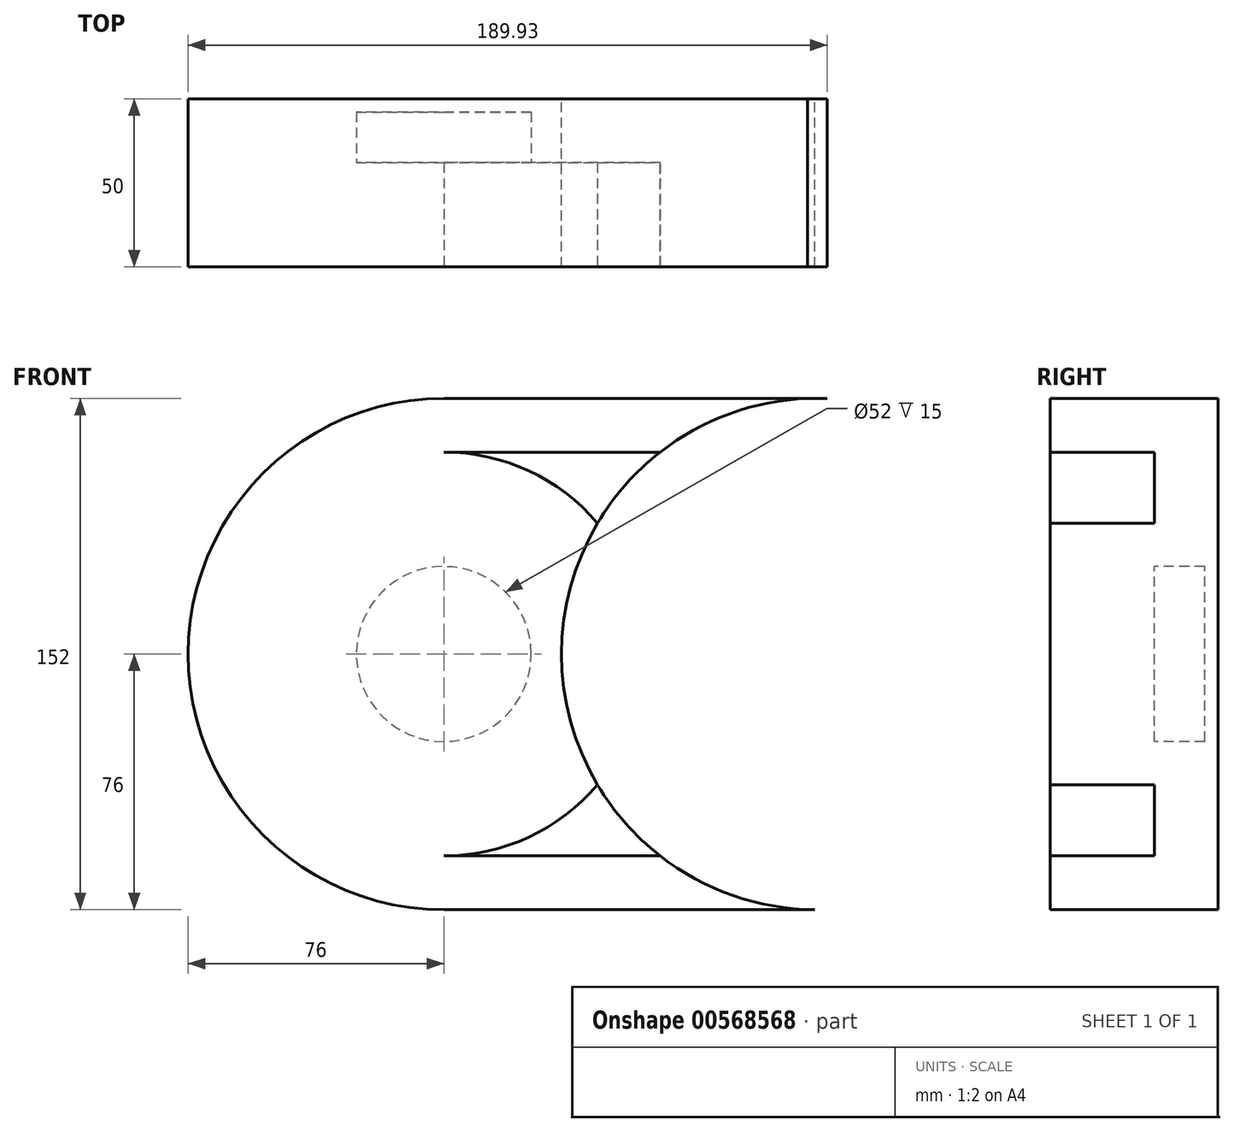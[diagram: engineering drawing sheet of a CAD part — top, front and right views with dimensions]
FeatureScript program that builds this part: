
annotation { "Feature Type Name" : "Feature", "Feature Type Description" : "" }
export const myFeature = defineFeature(function(context is Context, id is Id, definition is map)
    precondition{}
    {
        {
            var Q0;
            Q0=qCreatedBy(makeId("Front.planeOp"),FACE);
            var sketch = newSketch(context, id + "F0", { "sketchPlane" : qUnion([Q0])});
            skCircle(sketch, "E0", {"center": v(0, 0) * mm, "radius": 76 * mm});
            skCircle(sketch, "E1", {"center": v(111, 0) * mm, "radius": 76 * mm});
            skLineSegment(sketch, "E2", {"start": v(0, 76) * mm, "end": v(113.93, 75.94) * mm});
            skLineSegment(sketch, "E3", {"start": v(111.66, -76) * mm, "end": v(0, -76) * mm});
            skLineSegment(sketch, "E4", {"start": v(0, 0) * mm, "end": v(111, 0) * mm, "construction": true});
            skSolve(sketch);
        }
        {
            var Q0;
            {var subQ0=sQuery(id+"F0.wireOp",EDGE,"E3");var subQ1=sQuery(id+"F0.wireOp",EDGE,"E0");var subQ2=makeQuery(id+"F0.imprint","INTERSECT",VERTEX,{"derivedFrom":[subQ1,subQ0]});Q0=makeQuery(id+"F0.imprint","IMPRINT",FACE,{"disambiguationData":[TD([[makeQuery(id+"F0.imprint","IMPRINT",EDGE,{"disambiguationData":[TD([[subQ2,-1.0]])],"derivedFrom":subQ1}),-1.0]])]});}
            var Q1;
            {var subQ0=sQuery(id+"F0.wireOp",EDGE,"E0");var subQ1=makeQuery(id+"F0.imprint","INTERSECT",VERTEX,{"derivedFrom":[subQ0,sQuery(id+"F0.wireOp",EDGE,"E2")]});Q1=makeQuery(id+"F0.imprint","IMPRINT",FACE,{"disambiguationData":[TD([[makeQuery(id+"F0.imprint","IMPRINT",EDGE,{"disambiguationData":[TD([[subQ1,1.0]])],"derivedFrom":subQ0}),1.0]])]});}
            var Q2;
            {var subQ0=sQuery(id+"F0.wireOp",EDGE,"E1");var subQ2=sQuery(id+"F0.wireOp",EDGE,"E0");var subQ6=makeQuery(id+"F0.imprint","INTERSECT",VERTEX,{"disambiguationData":[OD(0.0)],"derivedFrom":[subQ2,subQ0]});Q2=makeQuery(id+"F0.imprint","IMPRINT",FACE,{"disambiguationData":[TD([[makeQuery(id+"F0.imprint","IMPRINT",EDGE,{"disambiguationData":[TD([[subQ6,1.0]])],"derivedFrom":subQ2}),-1.0]])]});}
            var Q3;
            {var subQ0=sQuery(id+"F0.wireOp",EDGE,"E2");var subQ1=sQuery(id+"F0.wireOp",EDGE,"E1");var subQ2=makeQuery(id+"F0.imprint","INTERSECT",VERTEX,{"disambiguationData":[OD(0.0)],"derivedFrom":[subQ1,subQ0]});Q3=makeQuery(id+"F0.imprint","IMPRINT",FACE,{"disambiguationData":[TD([[makeQuery(id+"F0.imprint","IMPRINT",EDGE,{"disambiguationData":[TD([[subQ2,-1.0]])],"derivedFrom":subQ1}),1.0]])]});}
            var Q4;
            {var subQ0=sQuery(id+"F0.wireOp",EDGE,"E2");var subQ1=sQuery(id+"F0.wireOp",EDGE,"E0");var subQ2=makeQuery(id+"F0.imprint","INTERSECT",VERTEX,{"derivedFrom":[subQ1,subQ0]});Q4=makeQuery(id+"F0.imprint","IMPRINT",FACE,{"disambiguationData":[TD([[makeQuery(id+"F0.imprint","IMPRINT",EDGE,{"disambiguationData":[TD([[subQ2,1.0]])],"derivedFrom":subQ1}),-1.0]])]});}
            var Q5;
            {var subQ0=sQuery(id+"F0.wireOp",EDGE,"E1");var subQ1=sQuery(id+"F0.wireOp",EDGE,"E0");var subQ2=makeQuery(id+"F0.imprint","INTERSECT",VERTEX,{"disambiguationData":[OD(0.0)],"derivedFrom":[subQ1,subQ0]});Q5=makeQuery(id+"F0.imprint","IMPRINT",FACE,{"disambiguationData":[TD([[makeQuery(id+"F0.imprint","IMPRINT",EDGE,{"disambiguationData":[TD([[subQ2,1.0]])],"derivedFrom":subQ1}),1.0]])]});}
            extrude(context, id + "F1", {"entities" : qUnion([Q0, Q1, Q2, Q3, Q4, Q5]), "depth" : 50 * mm, "offsetDistance" : 25 * mm});
        }
        {
            var Q0;
            Q0=qCreatedBy(makeId("Front.planeOp"),FACE);
            cPlane(context, id + "F2", {"entities" : qUnion([Q0]), "cplaneType" : CPlaneType.OFFSET, "offset" : 19 * mm, "width" : 150 * mm, "height" : 150 * mm});
        }
        {
            var Q0;
            Q0=makeQuery(id+"F1.opExtrude","CAP_FACE",FACE,{"disambiguationData":[OSD([sQuery(id+"F0.wireOp",EDGE,"E0"),sQuery(id+"F0.wireOp",EDGE,"E1"),sQuery(id+"F0.wireOp",EDGE,"E2"),sQuery(id+"F0.wireOp",EDGE,"E3")])],"isStart":false});
            var sketch = newSketch(context, id + "F3", { "sketchPlane" : qUnion([Q0])});
            skCircle(sketch, "E5", {"center": v(0, 0) * mm, "radius": 60 * mm});
            skCircle(sketch, "E6", {"center": v(111, 0) * mm, "radius": 60 * mm});
            skLineSegment(sketch, "E7", {"start": v(0, 60) * mm, "end": v(112.48, 59.98) * mm});
            skLineSegment(sketch, "E8", {"start": v(0, -60) * mm, "end": v(114.63, -59.9) * mm});
            skSolve(sketch);
        }
        {
            var Q0;
            {var subQ1=sQuery(id+"F3.wireOp",EDGE,"E6");var subQ5=sQuery(id+"F3.wireOp",EDGE,"E5");var subQ8=makeQuery(id+"F3.imprint","INTERSECT",VERTEX,{"disambiguationData":[OD(0.0)],"derivedFrom":[subQ5,subQ1]});Q0=makeQuery(id+"F3.imprint","IMPRINT",FACE,{"disambiguationData":[TD([[makeQuery(id+"F3.imprint","IMPRINT",EDGE,{"disambiguationData":[TD([[subQ8,1.0]])],"derivedFrom":subQ5}),-1.0]])]});}
            var Q1;
            {var subQ0=sQuery(id+"F3.wireOp",EDGE,"E7");var subQ1=sQuery(id+"F3.wireOp",EDGE,"E5");var subQ2=makeQuery(id+"F3.imprint","INTERSECT",VERTEX,{"derivedFrom":[subQ1,subQ0]});Q1=makeQuery(id+"F3.imprint","IMPRINT",FACE,{"disambiguationData":[TD([[makeQuery(id+"F3.imprint","IMPRINT",EDGE,{"disambiguationData":[TD([[subQ2,1.0]])],"derivedFrom":subQ1}),-1.0]])]});}
            var Q2;
            {var subQ0=sQuery(id+"F3.wireOp",EDGE,"E6");var subQ1=sQuery(id+"F3.wireOp",EDGE,"E5");var subQ2=makeQuery(id+"F3.imprint","INTERSECT",VERTEX,{"disambiguationData":[OD(0.0)],"derivedFrom":[subQ1,subQ0]});Q2=makeQuery(id+"F3.imprint","IMPRINT",FACE,{"disambiguationData":[TD([[makeQuery(id+"F3.imprint","IMPRINT",EDGE,{"disambiguationData":[TD([[subQ2,1.0]])],"derivedFrom":subQ1}),1.0]])]});}
            var Q3;
            {var subQ0=sQuery(id+"F3.wireOp",EDGE,"E5");var subQ3=makeQuery(id+"F3.imprint","IMPRINT",VERTEX,{"disambiguationData":[OD(0.0)],"derivedFrom":subQ0});Q3=makeQuery(id+"F3.imprint","IMPRINT",FACE,{"disambiguationData":[TD([[makeQuery(id+"F3.imprint","IMPRINT",EDGE,{"disambiguationData":[TD([[subQ3,-1.0]])],"derivedFrom":subQ0}),1.0]])]});}
            var Q4;
            {var subQ0=sQuery(id+"F3.wireOp",EDGE,"E8");var subQ1=sQuery(id+"F3.wireOp",EDGE,"E5");var subQ2=makeQuery(id+"F3.imprint","INTERSECT",VERTEX,{"derivedFrom":[subQ1,subQ0]});Q4=makeQuery(id+"F3.imprint","IMPRINT",FACE,{"disambiguationData":[TD([[makeQuery(id+"F3.imprint","IMPRINT",EDGE,{"disambiguationData":[TD([[subQ2,-1.0]])],"derivedFrom":subQ1}),-1.0]])]});}
            extrude(context, id + "F4", {"entities" : qUnion([Q0, Q1, Q2, Q3, Q4]), "operationType" : NewBodyOperationType.REMOVE, "oppositeDirection" : true, "depth" : 31 * mm, "offsetDistance" : 25 * mm});
        }
        {
            var Q0;
            Q0=qCreatedBy(id+"F2.planeOp",FACE);
            var sketch = newSketch(context, id + "F5", { "sketchPlane" : qUnion([Q0])});
            skCircle(sketch, "E9", {"center": v(0, 0) * mm, "radius": 26 * mm});
            skSolve(sketch);
        }
        {
            var Q0;
            Q0=makeQuery(id+"F5.imprint","IMPRINT",FACE,{"disambiguationData":[TD([[makeQuery(id+"F5.imprint","IMPRINT",EDGE,{"derivedFrom":sQuery(id+"F5.wireOp",EDGE,"E9")}),1.0]])]});
            extrude(context, id + "F6", {"entities" : qUnion([Q0]), "operationType" : NewBodyOperationType.REMOVE, "oppositeDirection" : true, "depth" : 15 * mm, "offsetDistance" : 25 * mm});
        }
        {
            var Q0;
            Q0=qCreatedBy(makeId("Right.planeOp"),FACE);
            cPlane(context, id + "F7", {"entities" : qUnion([Q0]), "cplaneType" : CPlaneType.OFFSET, "offset" : 111 * mm, "width" : 150 * mm, "height" : 150 * mm});
        }
        {
            var Q0;
            Q0=qCreatedBy(id+"F7.planeOp",FACE);
            var sketch = newSketch(context, id + "F8", { "sketchPlane" : qUnion([Q0])});
            skLineSegment(sketch, "E10", {"start": v(0, 0) * mm, "end": v(-20, 0) * mm});
            skLineSegment(sketch, "E11", {"start": v(-20, 0) * mm, "end": v(-20, 23.5) * mm});
            skLineSegment(sketch, "E12", {"start": v(-20, 23.5) * mm, "end": v(-7, 23.5) * mm});
            skLineSegment(sketch, "E13", {"start": v(-7, 23.5) * mm, "end": v(-7, 18.5) * mm});
            skLineSegment(sketch, "E14", {"start": v(-7, 18.5) * mm, "end": v(-2, 18.5) * mm});
            skLineSegment(sketch, "E15", {"start": v(-2, 18.5) * mm, "end": v(-2, 11) * mm});
            skLineSegment(sketch, "E16", {"start": v(-2, 11) * mm, "end": v(0, 11) * mm});
            skLineSegment(sketch, "E17", {"start": v(0, 0) * mm, "end": v(-104.27, 0) * mm, "construction": true});
            skLineSegment(sketch, "E18", {"start": v(0, 11) * mm, "end": v(0, 0) * mm});
            skSolve(sketch);
        }
        {
            var Q0;
            Q0=makeQuery(id+"F8.imprint","IMPRINT",FACE,{"disambiguationData":[TD([[makeQuery(id+"F8.imprint","IMPRINT",EDGE,{"derivedFrom":sQuery(id+"F8.wireOp",EDGE,"E10")}),-1.0]])]});
            var Q1;
            Q1=sQuery(id+"F8.wireOp",EDGE,"E17");
            revolve(context, id + "F9", {"operationType" : NewBodyOperationType.REMOVE, "entities" : qUnion([Q0]), "axis" : qUnion([Q1]), "revolveType" : RevolveType.FULL, "oppositeDirection" : true});
        }
    });
